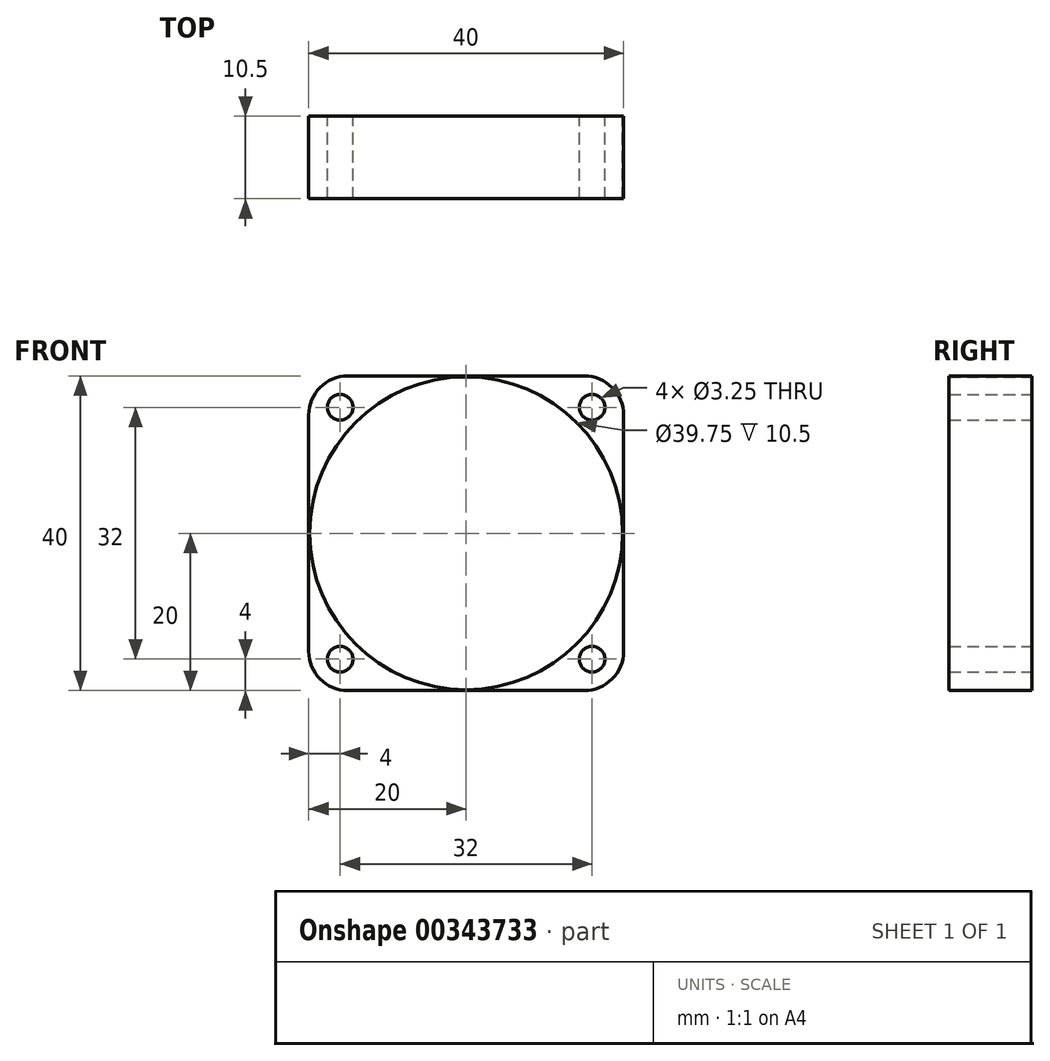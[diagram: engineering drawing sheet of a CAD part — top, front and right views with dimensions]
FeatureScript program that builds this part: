
annotation { "Feature Type Name" : "Feature", "Feature Type Description" : "" }
export const myFeature = defineFeature(function(context is Context, id is Id, definition is map)
    precondition{}
    {
        {
            var Q0;
            Q0=qCreatedBy(makeId("Front.planeOp"),FACE);
            var sketch = newSketch(context, id + "F0", { "sketchPlane" : qUnion([Q0])});
            skLineSegment(sketch, "E0.bottom", {"start": v(-15, 20) * mm, "end": v(15, 20) * mm});
            skLineSegment(sketch, "E0.top", {"start": v(-15, -20) * mm, "end": v(15, -20) * mm});
            skLineSegment(sketch, "E0.left", {"start": v(-20, 15) * mm, "end": v(-20, -15) * mm});
            skLineSegment(sketch, "E0.right", {"start": v(20, 15) * mm, "end": v(20, -15) * mm});
            skPoint(sketch, "E0.middle", {"position": v(0, 0) * mm});
            skCircle(sketch, "E1", {"center": v(-16, 16) * mm, "radius": 1.63 * mm});
            skCircle(sketch, "E2", {"center": v(16, 16) * mm, "radius": 1.63 * mm});
            skCircle(sketch, "E3", {"center": v(-16, -16) * mm, "radius": 1.63 * mm});
            skCircle(sketch, "E4", {"center": v(16, -16) * mm, "radius": 1.63 * mm});
            skPoint(sketch, "E5.visualSharp", {"position": v(-20, 20) * mm});
            skArc(sketch, "E5.filletArc", {"start": v(-15, 20) * mm, "mid": v(-18.54, 18.54) * mm, "end": v(-20, 15) * mm});
            skPoint(sketch, "E6.visualSharp", {"position": v(20, 20) * mm});
            skArc(sketch, "E6.filletArc", {"start": v(20, 15) * mm, "mid": v(18.54, 18.54) * mm, "end": v(15, 20) * mm});
            skPoint(sketch, "E7.visualSharp", {"position": v(20, -20) * mm});
            skArc(sketch, "E7.filletArc", {"start": v(15, -20) * mm, "mid": v(18.54, -18.54) * mm, "end": v(20, -15) * mm});
            skPoint(sketch, "E8.visualSharp", {"position": v(-20, -20) * mm});
            skArc(sketch, "E8.filletArc", {"start": v(-20, -15) * mm, "mid": v(-18.54, -18.54) * mm, "end": v(-15, -20) * mm});
            skCircle(sketch, "E9", {"center": v(0, 0) * mm, "radius": 19.88 * mm});
            skSolve(sketch);
        }
        {
            var Q0;
            Q0=makeQuery(id+"F0.imprint","IMPRINT",FACE,{"disambiguationData":[TD([[makeQuery(id+"F0.imprint","IMPRINT",EDGE,{"derivedFrom":sQuery(id+"F0.wireOp",EDGE,"E0.bottom")}),-1.0]])]});
            extrude(context, id + "F1", {"entities" : qUnion([Q0]), "depth" : 10.5 * mm});
        }
    });
